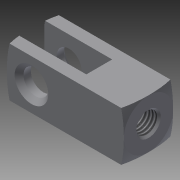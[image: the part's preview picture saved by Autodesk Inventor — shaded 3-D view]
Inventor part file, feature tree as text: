
AUTODESK INVENTOR PART (.ipt)
format: ipt  version: 2014 SP2 (Build 180246200, 246)  size: 200,192 bytes
history: native  units: in
note: dims shown in document units (in); Inventor stores cm internally (conversion verified against a paired STEP export)
features: other x126, sketch x7, revolve x4, extrude x2, thread x1, hole x1
ambient origin geometry x8: Origin, YZ Plane, XZ Plane, XY Plane, X Axis, Y Axis, Z Axis, Center Point
bodies: Solid1 (feature_tree)
feature tree (141):
  extrude  "Extrusion1"  Depth=0.5in TaperAngle=0.0deg
  extrude  "Extrusion2"  Depth=0.4207in TaperAngle=0.0deg
  revolve  "Revolution1"  Angle=360.0deg
  thread  "Thread1"  [1 undecoded]
  hole  "Hole1"  [1 undecoded]
  revolve  "Revolution2"  [1 undecoded]
  revolve  "Revolution3"  [1 undecoded]
  revolve  "Revolution4"  [1 undecoded]
  other  "dummy_XY"
  other  "dummy_YZ"
  other  "dummy_ZX"
  other  "dummy_X"
  other  "dummy_Y"
  other  "dummy_Z"
  other  "dummy_Center"
  other  "h1_XY"
  other  "h1_YZ"
  other  "h1_ZX"
  other  "h1_X"
  other  "h1_Y"
  other  "h1_Z"
  other  "h1_Center"
  other  "h2_XY"
  other  "h2_YZ"
  other  "h2_ZX"
  other  "h2_X"
  other  "h2_Y"
  other  "h2_Z"
  other  "h2_Center"
  other  "l1_XY"
  other  "l1_YZ"
  other  "l1_ZX"
  other  "l1_X"
  other  "l1_Y"
  other  "l1_Z"
  other  "l1_Center"
  other  "l11_XY"
  other  "l11_YZ"
  other  "l11_ZX"
  other  "l11_X"
  other  "l11_Y"
  other  "l11_Z"
  other  "l11_Center"
  other  "l12_XY"
  other  "l12_YZ"
  other  "l12_ZX"
  other  "l12_X"
  other  "l12_Y"
  other  "l12_Z"
  other  "l12_Center"
  other  "l2_XY"
  other  "l2_YZ"
  other  "l2_ZX"
  other  "l2_X"
  other  "l2_Y"
  other  "l2_Z"
  other  "l2_Center"
  other  "l21_XY"
  other  "l21_YZ"
  other  "l21_ZX"
  other  "l21_X"
  other  "l21_Y"
  other  "l21_Z"
  other  "l21_Center"
  other  "l22_XY"
  other  "l22_YZ"
  other  "l22_ZX"
  other  "l22_X"
  other  "l22_Y"
  other  "l22_Z"
  other  "l22_Center"
  other  "piston_rod_clevis_XY"
  other  "piston_rod_clevis_YZ"
  other  "piston_rod_clevis_ZX"
  other  "piston_rod_clevis_X"
  other  "piston_rod_clevis_Y"
  other  "piston_rod_clevis_Z"
  other  "piston_rod_clevis_Center"
  other  "rod_clevis_body_XY"
  other  "rod_clevis_body_YZ"
  other  "rod_clevis_body_ZX"
  other  "rod_clevis_body_X"
  other  "rod_clevis_body_Y"
  other  "rod_clevis_body_Z"
  other  "rod_clevis_body_Center"
  other  "th1_XY"
  other  "th1_YZ"
  other  "th1_ZX"
  other  "th1_X"
  other  "th1_Y"
  other  "th1_Z"
  other  "th1_Center"
  other  "th2_XY"
  other  "th2_YZ"
  other  "th2_ZX"
  other  "th2_X"
  other  "th2_Y"
  other  "th2_Z"
  other  "th2_Center"
  other  "to_cylinder_XY"
  other  "to_cylinder_YZ"
  other  "to_cylinder_ZX"
  other  "to_cylinder_X"
  other  "to_cylinder_Y"
  other  "to_cylinder_Z"
  other  "to_cylinder_Center"
  other  "w1_XY"
  other  "w1_YZ"
  other  "w1_ZX"
  other  "w1_X"
  other  "w1_Y"
  other  "w1_Z"
  other  "w1_Center"
  other  "w11_XY"
  other  "w11_YZ"
  other  "w11_ZX"
  other  "w11_X"
  other  "w11_Y"
  other  "w11_Z"
  other  "w11_Center"
  other  "w12_XY"
  other  "w12_YZ"
  other  "w12_ZX"
  other  "w12_X"
  other  "w12_Y"
  other  "w12_Z"
  other  "w12_Center"
  other  "w2_XY"
  other  "w2_YZ"
  other  "w2_ZX"
  other  "w2_X"
  other  "w2_Y"
  other  "w2_Z"
  other  "w2_Center"
  sketch  "Sketch_1"  dims[d0=0.5in d1=0.0in d2=0.5in d3=0.0in]
  sketch  "Sketch_2"  dims[d4=360.0deg d5=0.4207in d6=0.0in]
  sketch  "Sketch_3"  dims[d7=0.213in d8=0.75in d9=0.375in d10=0.25in d11=0.5635in d12=0.06in d13=0.0in d14=360.0deg d15=360.0deg]
  sketch  "Sketch5"  dims[d16=360.0deg d17=0.0in d18=0.0in]
  sketch  "Sketch_5"
  sketch  "Sketch_9"
  sketch  "Sketch_10"
note: 5 required parameter values undecoded (feature->parameter linkage not recoverable at this tier; creation-order binding heuristic only, values carry confidence <= 0.55)
